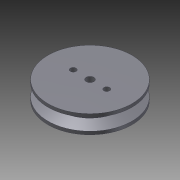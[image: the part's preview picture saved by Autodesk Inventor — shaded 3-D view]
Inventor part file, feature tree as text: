
AUTODESK INVENTOR PART (.ipt)
format: ipt  version: 2014 (Build 180170000, 170)  size: 131,584 bytes
history: native  units: mm (DEFAULTED — no unit token found)
features: other x3, fillet x2, extrude x2, sketch x2, pattern_linear x1
ambient origin geometry x8: Origin, YZ Plane, XZ Plane, XY Plane, X Axis, Y Axis, Z Axis, Center Point
bodies: Solid1 (feature_tree), Body (feature_tree)
feature tree (10):
  other  "Main Sketch"
  other  "Belt Plane"
  other  "Groove"
  fillet  "Fillet External"  Radius=10.6172mm
  fillet  "Fillet Internal"  Radius=5.934119mm
  pattern_linear  "Groove Pattern"  Spacing1=19.05mm  [1 undecoded]
  extrude  "Extrusion1"  TaperAngle=90.0deg  [1 undecoded]
  extrude  "Extrusion2"  TaperAngle=0.0deg  [1 undecoded]
  sketch  "Sketch2"  dims[d2=3.175mm]
  sketch  "Sketch3"  dims[d5=9.525mm d6=19.05mm d7=90.0deg d8=0.0mm d9=0.0mm d10=0.0mm d11=0.0mm d15=90.0deg d16=10.0mm d18=15.875mm d21=81.28mm d24=0.0mm d25=11.684mm d26=0.0mm d27=9.525mm d28=5.5mm d29=30.0mm d30=5.0mm d31=0.0mm d32=8.0mm d33=35.0mm d34=6.0mm d35=5.0mm d36=0.0mm]
note: 3 required parameter values undecoded (feature->parameter linkage not recoverable at this tier; creation-order binding heuristic only, values carry confidence <= 0.55)
